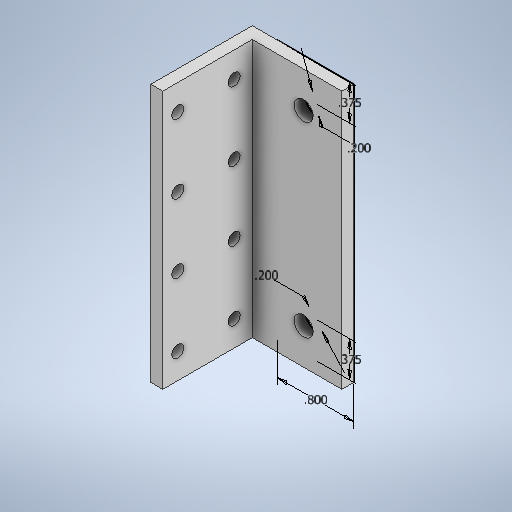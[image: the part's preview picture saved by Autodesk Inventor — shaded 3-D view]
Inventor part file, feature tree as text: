
AUTODESK INVENTOR PART (.ipt)
format: ipt  version: 2025.1 (Build 291241000, 241)  size: 304,640 bytes
history: native  units: in
note: dims shown in document units (in); Inventor stores cm internally (conversion verified against a paired STEP export)
features: extrude x6, sketch x6, direct_edit x3, move_body x3
ambient origin geometry x8: Origin, YZ Plane, XZ Plane, XY Plane, X Axis, Y Axis, Z Axis, Center Point
bodies: Solid1 (feature_tree)
feature tree (18):
  extrude  "Extrusion1"  Depth=1.0625in
  extrude  "Extrusion4"  Depth=0.125in
  direct_edit  "Direct Edit1"
  extrude  "Extrusion5"  Depth=0.535in
  direct_edit  "Direct Edit2"
  extrude  "Extrusion6"  Depth=0.125in
  direct_edit  "Direct Edit3"
  extrude  "Extrusion7"  Depth=0.125in
  extrude  "Extrusion8"  Depth=0.125in TaperAngle=0.0deg
  sketch  "Sketch1"  dims[d0=1.0625in d1=1.0625in]
  sketch  "Sketch4"  dims[d2=0.125in d4=0.125in]
  sketch  "Sketch5"  dims[d5=0.723in d6=0.0in d23=0.535in]
  sketch  "Sketch6"  dims[d24=0.315in d25=0.125in]
  sketch  "Sketch7"  dims[d26=0.59in d27=0.125in]
  sketch  "Sketch8"  dims[d28=0.723in d29=0.0in d30=0.0in d31=0.0in d32=0.535in d33=0.535in d34=0.315in d35=0.125in d36=0.59in d37=0.125in d38=0.723in d39=0.0in d40=0.0in d41=0.0in d42=0.7225in d43=0.535in d44=0.315in d45=0.125in d46=0.59in d47=0.125in d48=0.723in d49=0.0in d50=0.0in d51=0.0in d52=0.7225in d53=0.535in d54=0.315in d55=0.125in d56=0.59in d57=0.125in d58=0.723in d59=0.0in d60=0.8in d61=0.375in d62=0.375in d63=0.2in d64=0.2in d65=0.723in d66=0.0in]
  move_body  "Move1"
  move_body  "Move2"
  move_body  "Move3"
